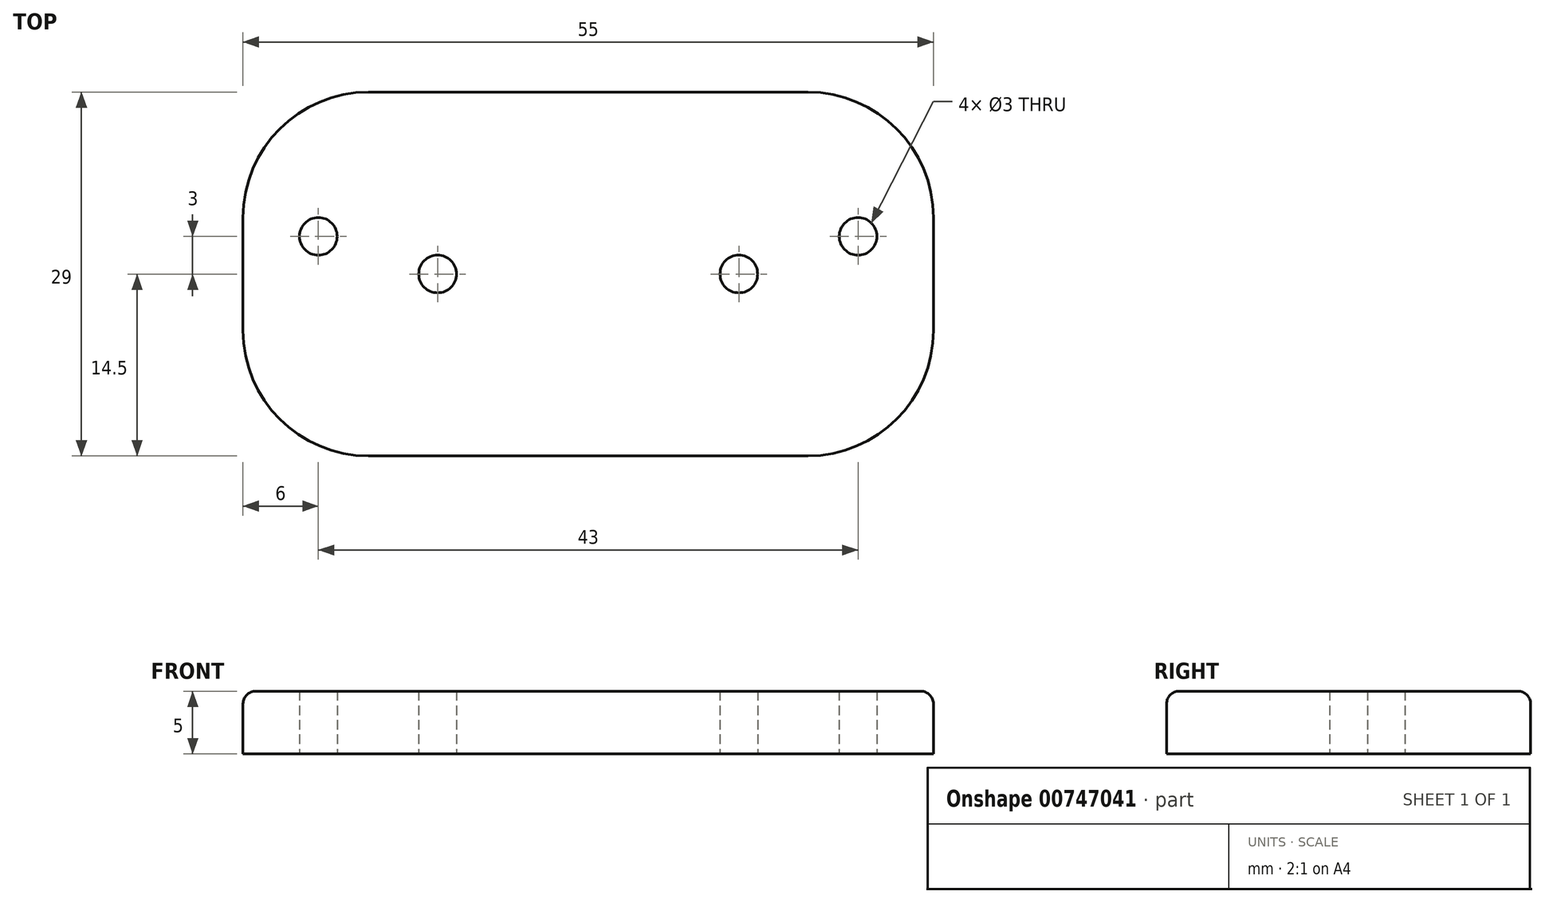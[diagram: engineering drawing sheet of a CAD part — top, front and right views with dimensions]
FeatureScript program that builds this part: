
annotation { "Feature Type Name" : "Feature", "Feature Type Description" : "" }
export const myFeature = defineFeature(function(context is Context, id is Id, definition is map)
    precondition{}
    {
        {
            var Q0;
            Q0=qCreatedBy(makeId("Top.planeOp"),FACE);
            var sketch = newSketch(context, id + "F0", { "sketchPlane" : qUnion([Q0])});
            skLineSegment(sketch, "E0.bottom", {"start": v(-17.5, 14.5) * mm, "end": v(17.5, 14.5) * mm});
            skLineSegment(sketch, "E0.top", {"start": v(-17.5, -14.5) * mm, "end": v(17.5, -14.5) * mm});
            skLineSegment(sketch, "E0.left", {"start": v(-27.5, 4.5) * mm, "end": v(-27.5, -4.5) * mm});
            skLineSegment(sketch, "E0.right", {"start": v(27.5, 4.5) * mm, "end": v(27.5, -4.5) * mm});
            skPoint(sketch, "E1.visualSharp", {"position": v(-27.5, 14.5) * mm});
            skArc(sketch, "E1.filletArc", {"start": v(-17.5, 14.5) * mm, "mid": v(-24.57, 11.57) * mm, "end": v(-27.5, 4.5) * mm});
            skPoint(sketch, "E2.visualSharp", {"position": v(27.5, 14.5) * mm});
            skArc(sketch, "E2.filletArc", {"start": v(27.5, 4.5) * mm, "mid": v(24.57, 11.57) * mm, "end": v(17.5, 14.5) * mm});
            skPoint(sketch, "E3.visualSharp", {"position": v(27.5, -14.5) * mm});
            skArc(sketch, "E3.filletArc", {"start": v(17.5, -14.5) * mm, "mid": v(24.57, -11.57) * mm, "end": v(27.5, -4.5) * mm});
            skPoint(sketch, "E4.visualSharp", {"position": v(-27.5, -14.5) * mm});
            skArc(sketch, "E4.filletArc", {"start": v(-27.5, -4.5) * mm, "mid": v(-24.57, -11.57) * mm, "end": v(-17.5, -14.5) * mm});
            skPoint(sketch, "E5", {"position": v(-21.5, 3) * mm});
            skPoint(sketch, "E6", {"position": v(21.5, 3) * mm});
            skPoint(sketch, "E7", {"position": v(-12, 0) * mm});
            skPoint(sketch, "E8", {"position": v(12, 0) * mm});
            skSolve(sketch);
        }
        {
            var Q0;
            Q0 = qSketchRegion(id + "F0", true);
            extrude(context, id + "F1", {"entities" : qUnion([Q0]), "depth" : 5 * mm, "offsetDistance" : 25 * mm});
        }
        {
            var Q0;
            Q0=makeQuery(id+"F1.opExtrude","CAP_FACE",FACE,{"disambiguationData":[OSD([sQuery(id+"F0.wireOp",EDGE,"E0.bottom"),sQuery(id+"F0.wireOp",EDGE,"E0.top"),sQuery(id+"F0.wireOp",EDGE,"E0.left"),sQuery(id+"F0.wireOp",EDGE,"E0.right"),sQuery(id+"F0.wireOp",EDGE,"E1.filletArc"),sQuery(id+"F0.wireOp",EDGE,"E2.filletArc"),sQuery(id+"F0.wireOp",EDGE,"E3.filletArc"),sQuery(id+"F0.wireOp",EDGE,"E4.filletArc")])],"isStart":false});
            fillet(context, id + "F2", {"entities" : qUnion([Q0]), "radius" : 1 * mm, "tangentPropagation" : true, "allowEdgeOverflow" : false});
        }
        {
            var Q0;
            Q0=sQuery(id+"F0.wireOp",VERTEX,"E5");
            var Q1;
            Q1=sQuery(id+"F0.wireOp",VERTEX,"E6");
            var Q2;
            Q2=makeQuery(id+"F1.opExtrude","SWEPT_BODY",BODY,{"disambiguationData":[OSD([sQuery(id+"F0.wireOp",EDGE,"E0.bottom"),sQuery(id+"F0.wireOp",EDGE,"E0.top"),sQuery(id+"F0.wireOp",EDGE,"E0.left"),sQuery(id+"F0.wireOp",EDGE,"E0.right"),sQuery(id+"F0.wireOp",EDGE,"E1.filletArc"),sQuery(id+"F0.wireOp",EDGE,"E2.filletArc"),sQuery(id+"F0.wireOp",EDGE,"E3.filletArc"),sQuery(id+"F0.wireOp",EDGE,"E4.filletArc")])]});
            hole(context, id + "F3", {"style" : HoleStyle.SIMPLE, "endStyle" : HoleEndStyle.THROUGH, "oppositeDirection" : true, "holeDiameter" : 3 * mm, "majorDiameter" : 5 * mm, "isTappedThrough" : true, "tappedDepth" : 12 * mm, "tapClearance" : 3, "startFromSketch" : true, "locations" : qUnion([Q0, Q1]), "scope" : qUnion([Q2])});
        }
        {
            var Q0;
            Q0=sQuery(id+"F0.wireOp",VERTEX,"E7");
            var Q1;
            Q1=sQuery(id+"F0.wireOp",VERTEX,"E8");
            var Q2;
            Q2=makeQuery(id+"F1.opExtrude","SWEPT_BODY",BODY,{"disambiguationData":[OSD([sQuery(id+"F0.wireOp",EDGE,"E0.bottom"),sQuery(id+"F0.wireOp",EDGE,"E0.top"),sQuery(id+"F0.wireOp",EDGE,"E0.left"),sQuery(id+"F0.wireOp",EDGE,"E0.right"),sQuery(id+"F0.wireOp",EDGE,"E1.filletArc"),sQuery(id+"F0.wireOp",EDGE,"E2.filletArc"),sQuery(id+"F0.wireOp",EDGE,"E3.filletArc"),sQuery(id+"F0.wireOp",EDGE,"E4.filletArc")])]});
            hole(context, id + "F4", {"style" : HoleStyle.SIMPLE, "endStyle" : HoleEndStyle.THROUGH, "oppositeDirection" : true, "holeDiameter" : 3 * mm, "majorDiameter" : 5 * mm, "isTappedThrough" : true, "tappedDepth" : 12 * mm, "tapClearance" : 3, "startFromSketch" : true, "locations" : qUnion([Q0, Q1]), "scope" : qUnion([Q2])});
        }
    });
